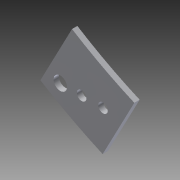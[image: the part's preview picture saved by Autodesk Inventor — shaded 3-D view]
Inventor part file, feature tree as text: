
AUTODESK INVENTOR PART (.ipt)
format: ipt  version: 2014 SP1 (Build 180222100, 222)  size: 103,936 bytes
history: native  units: in
note: dims shown in document units (in); Inventor stores cm internally (conversion verified against a paired STEP export)
features: extrude x1, sketch x1
ambient origin geometry x8: Origin, YZ Plane, XZ Plane, XY Plane, X Axis, Y Axis, Z Axis, Center Point
bodies: Solid1 (feature_tree)
feature tree (2):
  extrude  "Extrusion1"  Depth=12.5876in
  sketch  "Sketch1"  dims[d0=11.0in d1=12.5876in d2=1.0in d3=1.5915in d4=1.5915in d8=1.2353in d9=0.1732in d10=0.7318in d12=0.125in d13=0.0in d14=0.2244in d15=0.315in]
